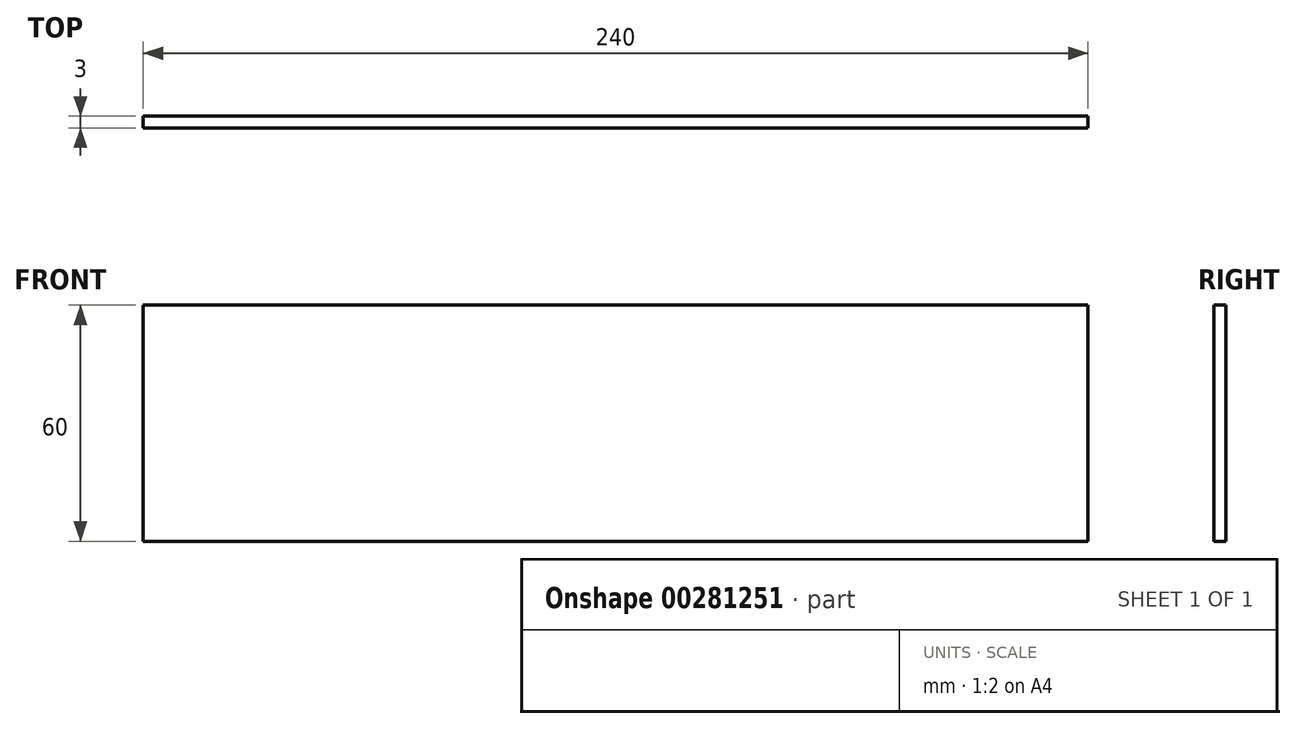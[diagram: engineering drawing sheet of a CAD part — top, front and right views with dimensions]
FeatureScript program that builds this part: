
annotation { "Feature Type Name" : "Feature", "Feature Type Description" : "" }
export const myFeature = defineFeature(function(context is Context, id is Id, definition is map)
    precondition{}
    {
        {
            var Q0;
            Q0=qCreatedBy(makeId("Front.planeOp"),FACE);
            var sketch = newSketch(context, id + "F0", { "sketchPlane" : qUnion([Q0])});
            skLineSegment(sketch, "E0.bottom", {"start": v(120, -30) * mm, "end": v(-120, -30) * mm});
            skLineSegment(sketch, "E0.top", {"start": v(120, 30) * mm, "end": v(-120, 30) * mm});
            skLineSegment(sketch, "E0.left", {"start": v(120, -30) * mm, "end": v(120, 30) * mm});
            skLineSegment(sketch, "E0.right", {"start": v(-120, -30) * mm, "end": v(-120, 30) * mm});
            skPoint(sketch, "E0.middle", {"position": v(0, 0) * mm});
            skSolve(sketch);
        }
        {
            var Q0;
            Q0=qSketchRegion(id+"F0",true);
            extrude(context, id + "F1", {"entities" : qUnion([Q0]), "depth" : 3 * mm});
        }
    });
